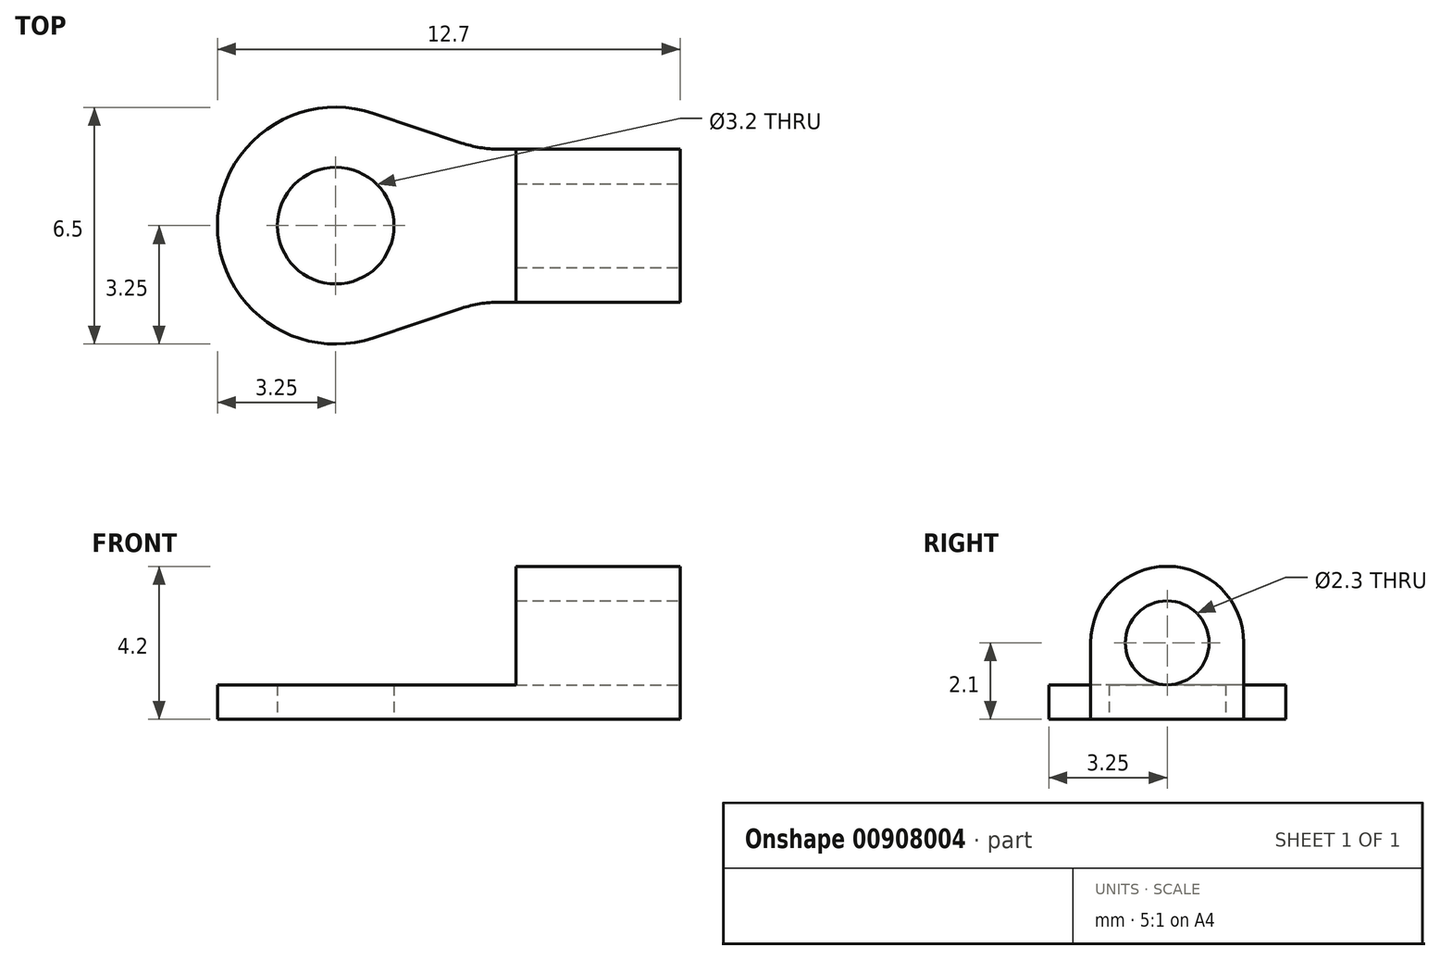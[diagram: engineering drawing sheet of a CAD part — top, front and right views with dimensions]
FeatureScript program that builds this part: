
annotation { "Feature Type Name" : "Feature", "Feature Type Description" : "" }
export const myFeature = defineFeature(function(context is Context, id is Id, definition is map)
    precondition{}
    {
        {
            var Q0;
            Q0=qCreatedBy(makeId("Top.planeOp"),FACE);
            var sketch = newSketch(context, id + "F0", { "sketchPlane" : qUnion([Q0])});
            skLineSegment(sketch, "E0.left", {"start": v(0, 3.25) * mm, "end": v(0, 3.25) * mm});
            skLineSegment(sketch, "E0.right", {"start": v(12.7, 1.15) * mm, "end": v(12.7, 5.35) * mm});
            skPoint(sketch, "E1.visualSharp", {"position": v(0, 6.5) * mm});
            skArc(sketch, "E1.filletArc", {"start": v(3.25, 6.5) * mm, "mid": v(0.95, 5.55) * mm, "end": v(0, 3.25) * mm});
            skPoint(sketch, "E2.visualSharp", {"position": v(0, 0) * mm});
            skArc(sketch, "E2.filletArc", {"start": v(0, 3.25) * mm, "mid": v(0.95, 0.95) * mm, "end": v(3.25, 0) * mm});
            skLineSegment(sketch, "E3.bottom", {"start": v(12.7, 1.15) * mm, "end": v(7.73, 1.15) * mm});
            skLineSegment(sketch, "E3.top", {"start": v(12.7, 5.35) * mm, "end": v(8.2, 5.35) * mm});
            skPoint(sketch, "E3.middle", {"position": v(12.7, 3.25) * mm});
            skArc(sketch, "E4", {"start": v(4.29, 6.33) * mm, "mid": v(0, 3.25) * mm, "end": v(4.29, 0.17) * mm});
            skCircle(sketch, "E5", {"center": v(3.25, 3.25) * mm, "radius": 1.6 * mm});
            skLineSegment(sketch, "E6", {"start": v(8.2, 5.35) * mm, "end": v(7.73, 5.35) * mm});
            skLineSegment(sketch, "E7", {"start": v(6.7, 0.98) * mm, "end": v(4.29, 0.17) * mm});
            skLineSegment(sketch, "E8", {"start": v(6.7, 5.52) * mm, "end": v(4.29, 6.33) * mm});
            skPoint(sketch, "E9.orphan", {"position": v(17.2, 5.35) * mm});
            skPoint(sketch, "E10.orphan", {"position": v(17.2, 1.15) * mm});
            skPoint(sketch, "E3.right.start.orphan", {"position": v(8.2, 1.15) * mm});
            skPoint(sketch, "E11.visualSharp", {"position": v(7.2, 5.35) * mm});
            skArc(sketch, "E11.filletArc", {"start": v(6.7, 5.52) * mm, "mid": v(7.2, 5.4) * mm, "end": v(7.73, 5.35) * mm});
            skPoint(sketch, "E12.visualSharp", {"position": v(7.2, 1.15) * mm});
            skArc(sketch, "E12.filletArc", {"start": v(7.73, 1.15) * mm, "mid": v(7.2, 1.1) * mm, "end": v(6.7, 0.98) * mm});
            skPoint(sketch, "E13.orphan", {"position": v(12.7, 6.5) * mm});
            skPoint(sketch, "E0.bottom.end.orphan", {"position": v(12.7, 0) * mm});
            skSolve(sketch);
        }
        {
            var Q0;
            Q0=makeQuery(id+"F0.imprint","IMPRINT",FACE,{"disambiguationData":[TD([[makeQuery(id+"F0.imprint","IMPRINT",EDGE,{"derivedFrom":sQuery(id+"F0.wireOp",EDGE,"E0.right")}),1.0]])]});
            extrude(context, id + "F1", {"entities" : qUnion([Q0]), "depth" : 0.95 * mm, "offsetDistance" : 25 * mm});
        }
        {
            var Q0;
            Q0=makeQuery(id+"F1.opExtrude","CAP_FACE",FACE,{"disambiguationData":[OSD([sQuery(id+"F0.wireOp",EDGE,"E0.right"),sQuery(id+"F0.wireOp",EDGE,"E3.bottom"),sQuery(id+"F0.wireOp",EDGE,"E3.top"),sQuery(id+"F0.wireOp",EDGE,"E4"),sQuery(id+"F0.wireOp",EDGE,"E5"),sQuery(id+"F0.wireOp",EDGE,"E6"),sQuery(id+"F0.wireOp",EDGE,"E7"),sQuery(id+"F0.wireOp",EDGE,"E8"),sQuery(id+"F0.wireOp",EDGE,"E11.filletArc"),sQuery(id+"F0.wireOp",EDGE,"E12.filletArc")])],"isStart":false});
            var sketch = newSketch(context, id + "F2", { "sketchPlane" : qUnion([Q0])});
            skLineSegment(sketch, "E14.bottom", {"start": v(12.7, 5.35) * mm, "end": v(8.2, 5.35) * mm});
            skLineSegment(sketch, "E14.top", {"start": v(12.7, 1.15) * mm, "end": v(8.2, 1.15) * mm});
            skLineSegment(sketch, "E14.left", {"start": v(12.7, 5.35) * mm, "end": v(12.7, 1.15) * mm});
            skLineSegment(sketch, "E14.right", {"start": v(8.2, 5.35) * mm, "end": v(8.2, 1.15) * mm});
            skSolve(sketch);
        }
        {
            var Q0;
            Q0=makeQuery(id+"F2.imprint","IMPRINT",FACE,{"disambiguationData":[TD([[makeQuery(id+"F2.imprint","IMPRINT",EDGE,{"derivedFrom":sQuery(id+"F2.wireOp",EDGE,"E14.bottom")}),1.0]])]});
            extrude(context, id + "F3", {"entities" : qUnion([Q0]), "operationType" : NewBodyOperationType.ADD, "depth" : 3.25 * mm, "offsetDistance" : 25 * mm});
        }
        {
            var Q0;
            Q0=makeQuery(id+"F3.opExtrude","CAP_EDGE",EDGE,{"disambiguationData":[OSD([sQuery(id+"F2.wireOp",EDGE,"E14.bottom")])],"isStart":false});
            var Q1;
            Q1=makeQuery(id+"F3.opExtrude","CAP_EDGE",EDGE,{"disambiguationData":[OSD([sQuery(id+"F2.wireOp",EDGE,"E14.top")])],"isStart":false});
            fillet(context, id + "F4", {"entities" : qUnion([Q0, Q1]), "radius" : 2.1 * mm, "tangentPropagation" : true, "allowEdgeOverflow" : false});
        }
        {
            var Q0;
            Q0=makeQuery(id+"F3.boolean.opBoolean","MERGE",FACE,{"derivedFrom":[makeQuery(id+"F1.opExtrude","SWEPT_FACE",FACE,{"disambiguationData":[OSD([sQuery(id+"F0.wireOp",EDGE,"E0.right")])]}),makeQuery(id+"F3.opExtrude","SWEPT_FACE",FACE,{"disambiguationData":[OSD([sQuery(id+"F2.wireOp",EDGE,"E14.left")])]})]});
            var sketch = newSketch(context, id + "F5", { "sketchPlane" : qUnion([Q0])});
            skCircle(sketch, "E15", {"center": v(3.25, 2.1) * mm, "radius": 1.15 * mm});
            skSolve(sketch);
        }
        {
            var Q0;
            Q0=makeQuery(id+"F5.imprint","IMPRINT",FACE,{"disambiguationData":[TD([[makeQuery(id+"F5.imprint","IMPRINT",EDGE,{"derivedFrom":sQuery(id+"F5.wireOp",EDGE,"E15")}),1.0]])]});
            extrude(context, id + "F6", {"entities" : qUnion([Q0]), "operationType" : NewBodyOperationType.REMOVE, "oppositeDirection" : true, "depth" : 25 * mm, "offsetDistance" : 25 * mm});
        }
    });
